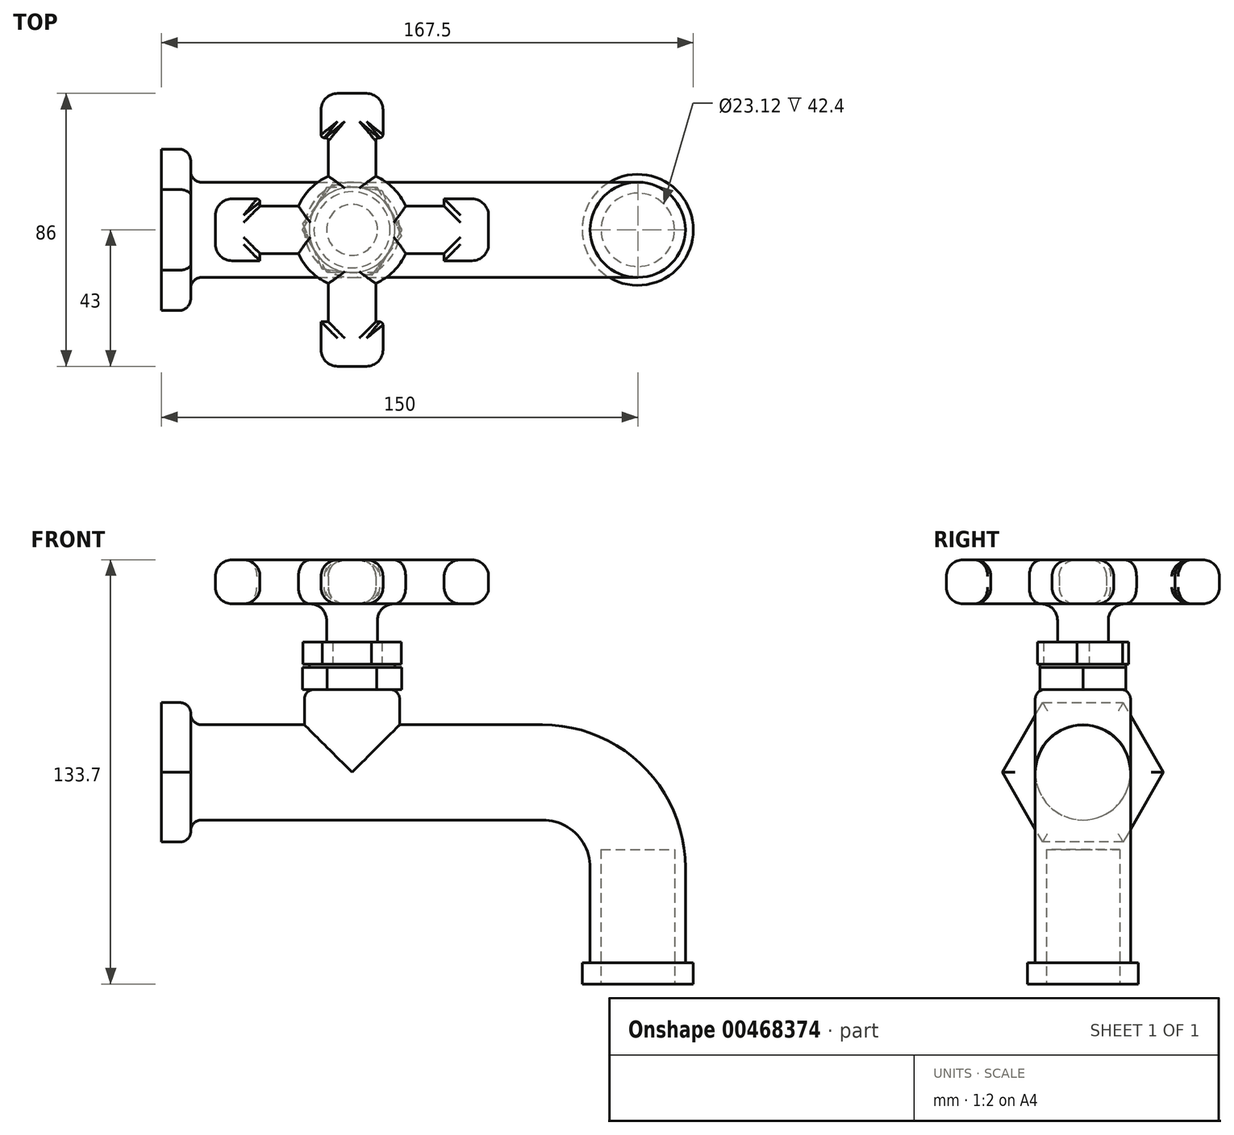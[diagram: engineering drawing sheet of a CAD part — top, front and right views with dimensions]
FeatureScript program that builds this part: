
annotation { "Feature Type Name" : "Feature", "Feature Type Description" : "" }
export const myFeature = defineFeature(function(context is Context, id is Id, definition is map)
    precondition{}
    {
        {
            var Q0;
            Q0=qCreatedBy(makeId("Front.planeOp"),FACE);
            var sketch = newSketch(context, id + "F0", { "sketchPlane" : qUnion([Q0])});
            skLineSegment(sketch, "E0", {"start": v(-60, 0) * mm, "end": v(60, 0) * mm});
            skLineSegment(sketch, "E1", {"start": v(90, -30) * mm, "end": v(90, -60) * mm});
            skPoint(sketch, "E2.visualSharp", {"position": v(90, 0) * mm});
            skArc(sketch, "E2.filletArc", {"start": v(90, -30) * mm, "mid": v(81.21, -8.79) * mm, "end": v(60, 0) * mm});
            skSolve(sketch);
        }
        {
            var Q0;
            Q0=sQuery(id+"F0.wireOp",VERTEX,"E0.start");
            var Q1;
            Q1=qCreatedBy(makeId("Right.planeOp"),FACE);
            cPlane(context, id + "F1", {"entities" : qUnion([Q0, Q1]), "cplaneType" : CPlaneType.PLANE_POINT, "offset" : 25 * mm, "width" : 150 * mm, "height" : 150 * mm});
        }
        {
            var Q0;
            Q0=qCreatedBy(id+"F1.planeOp",FACE);
            var sketch = newSketch(context, id + "F2", { "sketchPlane" : qUnion([Q0])});
            skCircle(sketch, "E3", {"center": v(0, 0) * mm, "radius": 15 * mm});
            skSolve(sketch);
        }
        {
            var Q0;
            Q0=makeQuery(id+"F2.imprint","IMPRINT",FACE,{"disambiguationData":[TD([[makeQuery(id+"F2.imprint","IMPRINT",EDGE,{"derivedFrom":sQuery(id+"F2.wireOp",EDGE,"E3")}),1.0]])]});
            var Q1;
            Q1=sQuery(id+"F0.wireOp",EDGE,"E0");
            var Q2;
            Q2=sQuery(id+"F0.wireOp",EDGE,"E2.filletArc");
            var Q3;
            Q3=sQuery(id+"F0.wireOp",EDGE,"E1");
            sweep(context, id + "F3", {"profiles" : qUnion([Q0]), "path" : qUnion([Q1, Q2, Q3])});
        }
        {
            var Q0;
            Q0=qCreatedBy(makeId("Top.planeOp"),FACE);
            var sketch = newSketch(context, id + "F4", { "sketchPlane" : qUnion([Q0])});
            skLineSegment(sketch, "E4.0", {"start": v(-60, 0) * mm, "end": v(60, 0) * mm, "construction": true});
            skCircle(sketch, "E5", {"center": v(0, 0) * mm, "radius": 15 * mm});
            skSolve(sketch);
        }
        {
            var Q0;
            Q0 = qSketchRegion(id + "F4", true);
            extrude(context, id + "F5", {"entities" : qUnion([Q0]), "operationType" : NewBodyOperationType.ADD, "depth" : 26.1 * mm});
        }
        {
            var Q0;
            Q0=makeQuery(id+"F5.opExtrude","CAP_FACE",FACE,{"disambiguationData":[OSD([sQuery(id+"F4.wireOp",EDGE,"E5")])],"isStart":false});
            fillet(context, id + "F6", {"entities" : qUnion([Q0]), "radius" : 3 * mm, "tangentPropagation" : true, "allowEdgeOverflow" : false});
        }
        {
            var Q0;
            Q0=makeQuery(id+"F5.opExtrude","CAP_FACE",FACE,{"disambiguationData":[OSD([sQuery(id+"F4.wireOp",EDGE,"E5")])],"isStart":false});
            var sketch = newSketch(context, id + "F7", { "sketchPlane" : qUnion([Q0])});
            skCircle(sketch, "E6.cCircle", {"center": v(0, 0) * mm, "radius": 13.5 * mm, "construction": true});
            skLineSegment(sketch, "E6.0", {"start": v(15.59, 0) * mm, "end": v(7.8, -13.5) * mm});
            skLineSegment(sketch, "E6.1", {"start": v(7.8, -13.5) * mm, "end": v(-7.8, -13.5) * mm});
            skLineSegment(sketch, "E6.2", {"start": v(-7.8, -13.5) * mm, "end": v(-15.59, 0) * mm});
            skLineSegment(sketch, "E6.3", {"start": v(-15.59, 0) * mm, "end": v(-7.8, 13.5) * mm});
            skLineSegment(sketch, "E6.4", {"start": v(-7.8, 13.5) * mm, "end": v(7.8, 13.5) * mm});
            skLineSegment(sketch, "E6.5", {"start": v(7.8, 13.5) * mm, "end": v(15.59, 0) * mm});
            skPoint(sketch, "E6.0.midPoint", {"position": v(11.7, -6.75) * mm});
            skSolve(sketch);
        }
        {
            var Q0;
            Q0 = qSketchRegion(id + "F7", true);
            extrude(context, id + "F8", {"entities" : qUnion([Q0]), "operationType" : NewBodyOperationType.ADD, "depth" : 7 * mm});
        }
        {
            var Q0;
            Q0=makeQuery(id+"F8.opExtrude","CAP_FACE",FACE,{"disambiguationData":[OSD([sQuery(id+"F7.wireOp",EDGE,"E6.0"),sQuery(id+"F7.wireOp",EDGE,"E6.1"),sQuery(id+"F7.wireOp",EDGE,"E6.2"),sQuery(id+"F7.wireOp",EDGE,"E6.3"),sQuery(id+"F7.wireOp",EDGE,"E6.4"),sQuery(id+"F7.wireOp",EDGE,"E6.5")])],"isStart":false});
            var sketch = newSketch(context, id + "F9", { "sketchPlane" : qUnion([Q0])});
            skCircle(sketch, "E7.0", {"center": v(0, 0) * mm, "radius": 13.5 * mm});
            skSolve(sketch);
        }
        {
            var Q0;
            Q0 = qSketchRegion(id + "F9", true);
            extrude(context, id + "F10", {"entities" : qUnion([Q0]), "operationType" : NewBodyOperationType.ADD, "depth" : 1 * mm});
        }
        {
            var Q0;
            Q0=makeQuery(id+"F10.opExtrude","CAP_FACE",FACE,{"disambiguationData":[OSD([sQuery(id+"F9.wireOp",EDGE,"E7.0")])],"isStart":false});
            var sketch = newSketch(context, id + "F11", { "sketchPlane" : qUnion([Q0])});
            skCircle(sketch, "E8.cCircle", {"center": v(0, 0) * mm, "radius": 13.5 * mm, "construction": true});
            skLineSegment(sketch, "E8.0", {"start": v(9.38, 12.45) * mm, "end": v(15.47, -1.9) * mm});
            skLineSegment(sketch, "E8.1", {"start": v(15.47, -1.9) * mm, "end": v(6.1, -14.35) * mm});
            skLineSegment(sketch, "E8.2", {"start": v(6.1, -14.35) * mm, "end": v(-9.38, -12.45) * mm});
            skLineSegment(sketch, "E8.3", {"start": v(-9.38, -12.45) * mm, "end": v(-15.47, 1.9) * mm});
            skLineSegment(sketch, "E8.4", {"start": v(-15.47, 1.9) * mm, "end": v(-6.1, 14.35) * mm});
            skLineSegment(sketch, "E8.5", {"start": v(-6.1, 14.35) * mm, "end": v(9.38, 12.45) * mm});
            skPoint(sketch, "E8.0.midPoint", {"position": v(12.42, 5.28) * mm});
            skSolve(sketch);
        }
        {
            var Q0;
            Q0 = qSketchRegion(id + "F11", true);
            extrude(context, id + "F12", {"entities" : qUnion([Q0]), "operationType" : NewBodyOperationType.ADD, "depth" : 7 * mm});
        }
        {
            var Q0;
            Q0=makeQuery(id+"F12.opExtrude","CAP_FACE",FACE,{"disambiguationData":[OSD([sQuery(id+"F11.wireOp",EDGE,"E8.0"),sQuery(id+"F11.wireOp",EDGE,"E8.1"),sQuery(id+"F11.wireOp",EDGE,"E8.2"),sQuery(id+"F11.wireOp",EDGE,"E8.3"),sQuery(id+"F11.wireOp",EDGE,"E8.4"),sQuery(id+"F11.wireOp",EDGE,"E8.5")])],"isStart":false});
            var sketch = newSketch(context, id + "F13", { "sketchPlane" : qUnion([Q0])});
            skCircle(sketch, "E9", {"center": v(0, 0) * mm, "radius": 8 * mm});
            skSolve(sketch);
        }
        {
            var Q0;
            Q0 = qSketchRegion(id + "F13", true);
            extrude(context, id + "F14", {"entities" : qUnion([Q0]), "operationType" : NewBodyOperationType.ADD, "depth" : 12 * mm});
        }
        {
            var Q0;
            Q0=makeQuery(id+"F14.opExtrude","CAP_FACE",FACE,{"disambiguationData":[OSD([sQuery(id+"F13.wireOp",EDGE,"E9")])],"isStart":false});
            var sketch = newSketch(context, id + "F15", { "sketchPlane" : qUnion([Q0])});
            skPoint(sketch, "E10.middle", {"position": v(0, 0) * mm});
            skLineSegment(sketch, "E11.bottom", {"start": v(-29, 7.47) * mm, "end": v(-16.88, 7.47) * mm});
            skLineSegment(sketch, "E11.top", {"start": v(-29, -7.47) * mm, "end": v(-16.88, -7.47) * mm});
            skLineSegment(sketch, "E12.left", {"start": v(-43, 9.74) * mm, "end": v(-43, -9.74) * mm});
            skLineSegment(sketch, "E12.right", {"start": v(-29, 9.74) * mm, "end": v(-29, 7.47) * mm});
            skLineSegment(sketch, "E13.left", {"start": v(43, 9.74) * mm, "end": v(43, -9.74) * mm});
            skLineSegment(sketch, "E13.right", {"start": v(29, 9.74) * mm, "end": v(29, 7.47) * mm});
            skArc(sketch, "E14", {"start": v(-16.88, -7.47) * mm, "mid": v(-13.05, -13.05) * mm, "end": v(-7.47, -16.88) * mm});
            skLineSegment(sketch, "E15.trimOffspring", {"start": v(16.88, 7.47) * mm, "end": v(29, 7.47) * mm});
            skLineSegment(sketch, "E16.trimOffspring", {"start": v(16.88, -7.47) * mm, "end": v(29, -7.47) * mm});
            skArc(sketch, "E17.trimOffspring", {"start": v(16.88, 7.47) * mm, "mid": v(13.05, 13.05) * mm, "end": v(7.47, 16.88) * mm});
            skLineSegment(sketch, "E18.trimOffspring", {"start": v(-29, -7.47) * mm, "end": v(-29, -9.74) * mm});
            skLineSegment(sketch, "E19.1.0", {"start": v(-7.47, -16.88) * mm, "end": v(-7.47, -29) * mm});
            skLineSegment(sketch, "E19.1.1", {"start": v(7.47, -16.88) * mm, "end": v(7.47, -29) * mm});
            skLineSegment(sketch, "E19.1.2", {"start": v(9.74, 43) * mm, "end": v(-9.74, 43) * mm});
            skLineSegment(sketch, "E19.1.4", {"start": v(9.74, -29) * mm, "end": v(7.47, -29) * mm});
            skArc(sketch, "E19.1.5", {"start": v(-7.47, 16.88) * mm, "mid": v(-13.05, 13.05) * mm, "end": v(-16.88, 7.47) * mm});
            skLineSegment(sketch, "E19.1.7", {"start": v(9.74, 29) * mm, "end": v(7.47, 29) * mm});
            skLineSegment(sketch, "E19.1.9", {"start": v(-7.47, 29) * mm, "end": v(-9.74, 29) * mm});
            skLineSegment(sketch, "E19.1.10", {"start": v(-7.47, 29) * mm, "end": v(-7.47, 16.88) * mm});
            skLineSegment(sketch, "E19.1.11", {"start": v(7.47, 29) * mm, "end": v(7.47, 16.88) * mm});
            skArc(sketch, "E19.1.18", {"start": v(7.47, -16.88) * mm, "mid": v(13.05, -13.05) * mm, "end": v(16.88, -7.47) * mm});
            skLineSegment(sketch, "E19.1.19", {"start": v(9.74, -43) * mm, "end": v(-9.74, -43) * mm});
            skLineSegment(sketch, "E19.1.20", {"start": v(-7.27, -29) * mm, "end": v(-9.74, -29) * mm});
            skLineSegment(sketch, "E19.1.23", {"start": v(-9.74, -29) * mm, "end": v(-7.27, -29) * mm});
            skLineSegment(sketch, "E19.anchor1", {"start": v(0, 0) * mm, "end": v(-43, -13) * mm, "construction": true});
            skLineSegment(sketch, "E19.anchor2", {"start": v(0, 0) * mm, "end": v(-13, 43) * mm, "construction": true});
            skLineSegment(sketch, "E20", {"start": v(29, -7.47) * mm, "end": v(29, -9.74) * mm});
            skLineSegment(sketch, "E21.bottom", {"start": v(43, 9.74) * mm, "end": v(29, 9.74) * mm});
            skLineSegment(sketch, "E21.top", {"start": v(43, -9.74) * mm, "end": v(29, -9.74) * mm});
            skLineSegment(sketch, "E22.trimOffspring", {"start": v(-29, 9.74) * mm, "end": v(-43, 9.74) * mm});
            skLineSegment(sketch, "E23.trimOffspring", {"start": v(-29, -9.74) * mm, "end": v(-43, -9.74) * mm});
            skLineSegment(sketch, "E24.left", {"start": v(9.74, 43) * mm, "end": v(9.74, 29) * mm});
            skLineSegment(sketch, "E24.right", {"start": v(-9.74, 43) * mm, "end": v(-9.74, 29) * mm});
            skLineSegment(sketch, "E25.trimOffspring", {"start": v(-9.74, -29) * mm, "end": v(-9.74, -43) * mm});
            skLineSegment(sketch, "E26.trimOffspring", {"start": v(9.74, -29) * mm, "end": v(9.74, -43) * mm});
            skSolve(sketch);
        }
        {
            var Q0;
            Q0 = qSketchRegion(id + "F15", true);
            extrude(context, id + "F16", {"entities" : qUnion([Q0]), "operationType" : NewBodyOperationType.ADD, "depth" : 13.9 * mm});
        }
        {
            var Q0;
            Q0=makeQuery(id+"F16.opExtrude","CAP_FACE",FACE,{"disambiguationData":[OSD([sQuery(id+"F15.wireOp",EDGE,"E11.bottom"),sQuery(id+"F15.wireOp",EDGE,"E11.top"),sQuery(id+"F15.wireOp",EDGE,"E12.right"),sQuery(id+"F15.wireOp",EDGE,"E13.right"),sQuery(id+"F15.wireOp",EDGE,"E15.trimOffspring"),sQuery(id+"F15.wireOp",EDGE,"E16.trimOffspring"),sQuery(id+"F15.wireOp",EDGE,"E18.trimOffspring"),sQuery(id+"F15.wireOp",EDGE,"E19.1.0"),sQuery(id+"F15.wireOp",EDGE,"E19.1.1"),sQuery(id+"F15.wireOp",EDGE,"E19.1.2"),sQuery(id+"F15.wireOp",EDGE,"E19.1.4"),sQuery(id+"F15.wireOp",EDGE,"E19.1.7"),sQuery(id+"F15.wireOp",EDGE,"E19.1.9"),sQuery(id+"F15.wireOp",EDGE,"E19.1.10"),sQuery(id+"F15.wireOp",EDGE,"E19.1.11"),sQuery(id+"F15.wireOp",EDGE,"E19.1.19"),sQuery(id+"F15.wireOp",EDGE,"E19.1.23"),sQuery(id+"F15.wireOp",EDGE,"E19.1.5"),sQuery(id+"F15.wireOp",EDGE,"E17.trimOffspring"),sQuery(id+"F15.wireOp",EDGE,"E19.1.18"),sQuery(id+"F15.wireOp",EDGE,"E14"),sQuery(id+"F15.wireOp",EDGE,"E20"),sQuery(id+"F15.wireOp",EDGE,"E21.bottom"),sQuery(id+"F15.wireOp",EDGE,"E21.top"),sQuery(id+"F15.wireOp",EDGE,"E13.left"),sQuery(id+"F15.wireOp",EDGE,"E12.left"),sQuery(id+"F15.wireOp",EDGE,"E22.trimOffspring"),sQuery(id+"F15.wireOp",EDGE,"E23.trimOffspring"),sQuery(id+"F15.wireOp",EDGE,"E24.left"),sQuery(id+"F15.wireOp",EDGE,"E24.right"),sQuery(id+"F15.wireOp",EDGE,"E25.trimOffspring"),sQuery(id+"F15.wireOp",EDGE,"E26.trimOffspring")])],"isStart":true});
            var Q1;
            Q1=makeQuery(id+"F16.opExtrude","CAP_FACE",FACE,{"disambiguationData":[OSD([sQuery(id+"F15.wireOp",EDGE,"E11.bottom"),sQuery(id+"F15.wireOp",EDGE,"E11.top"),sQuery(id+"F15.wireOp",EDGE,"E12.right"),sQuery(id+"F15.wireOp",EDGE,"E13.right"),sQuery(id+"F15.wireOp",EDGE,"E15.trimOffspring"),sQuery(id+"F15.wireOp",EDGE,"E16.trimOffspring"),sQuery(id+"F15.wireOp",EDGE,"E18.trimOffspring"),sQuery(id+"F15.wireOp",EDGE,"E19.1.0"),sQuery(id+"F15.wireOp",EDGE,"E19.1.1"),sQuery(id+"F15.wireOp",EDGE,"E19.1.2"),sQuery(id+"F15.wireOp",EDGE,"E19.1.4"),sQuery(id+"F15.wireOp",EDGE,"E19.1.7"),sQuery(id+"F15.wireOp",EDGE,"E19.1.9"),sQuery(id+"F15.wireOp",EDGE,"E19.1.10"),sQuery(id+"F15.wireOp",EDGE,"E19.1.11"),sQuery(id+"F15.wireOp",EDGE,"E19.1.19"),sQuery(id+"F15.wireOp",EDGE,"E19.1.23"),sQuery(id+"F15.wireOp",EDGE,"E19.1.5"),sQuery(id+"F15.wireOp",EDGE,"E17.trimOffspring"),sQuery(id+"F15.wireOp",EDGE,"E19.1.18"),sQuery(id+"F15.wireOp",EDGE,"E14"),sQuery(id+"F15.wireOp",EDGE,"E20"),sQuery(id+"F15.wireOp",EDGE,"E21.bottom"),sQuery(id+"F15.wireOp",EDGE,"E21.top"),sQuery(id+"F15.wireOp",EDGE,"E13.left"),sQuery(id+"F15.wireOp",EDGE,"E12.left"),sQuery(id+"F15.wireOp",EDGE,"E22.trimOffspring"),sQuery(id+"F15.wireOp",EDGE,"E23.trimOffspring"),sQuery(id+"F15.wireOp",EDGE,"E24.left"),sQuery(id+"F15.wireOp",EDGE,"E24.right"),sQuery(id+"F15.wireOp",EDGE,"E25.trimOffspring"),sQuery(id+"F15.wireOp",EDGE,"E26.trimOffspring")])],"isStart":false});
            var Q2;
            Q2=makeQuery(id+"F16.opExtrude","SWEPT_FACE",FACE,{"disambiguationData":[OSD([sQuery(id+"F15.wireOp",EDGE,"E19.1.19")])]});
            var Q3;
            Q3=makeQuery(id+"F16.opExtrude","SWEPT_FACE",FACE,{"disambiguationData":[OSD([sQuery(id+"F15.wireOp",EDGE,"E12.left")])]});
            var Q4;
            Q4=makeQuery(id+"F16.opExtrude","SWEPT_FACE",FACE,{"disambiguationData":[OSD([sQuery(id+"F15.wireOp",EDGE,"E19.1.2")])]});
            var Q5;
            Q5=makeQuery(id+"F16.opExtrude","SWEPT_FACE",FACE,{"disambiguationData":[OSD([sQuery(id+"F15.wireOp",EDGE,"E13.left")])]});
            fillet(context, id + "F17", {"entities" : qUnion([Q0, Q1, Q2, Q3, Q4, Q5]), "radius" : 5.2 * mm, "tangentPropagation" : true, "allowEdgeOverflow" : false});
        }
        {
            var Q0;
            {var subQ0=sQuery(id+"F15.wireOp",EDGE,"E22.trimOffspring");Q0=makeQuery(id+"F17.opFillet","BLEND_FACE",FACE,{"disambiguationData":[OSD([subQ0]),TDD([makeQuery(id+"F16.opExtrude","CAP_EDGE",EDGE,{"disambiguationData":[OSD([subQ0])],"isStart":false})])]});}
            var Q1;
            {var subQ0=sQuery(id+"F15.wireOp",EDGE,"E26.trimOffspring");Q1=makeQuery(id+"F17.opFillet","BLEND_FACE",FACE,{"disambiguationData":[OSD([subQ0]),TDD([makeQuery(id+"F16.opExtrude","CAP_EDGE",EDGE,{"disambiguationData":[OSD([subQ0])],"isStart":false})])]});}
            var Q2;
            Q2=makeQuery(id+"F16.opExtrude","SWEPT_FACE",FACE,{"disambiguationData":[OSD([sQuery(id+"F15.wireOp",EDGE,"E19.1.7")])]});
            var Q3;
            {var subQ0=sQuery(id+"F15.wireOp",EDGE,"E19.1.9");Q3=makeQuery(id+"F17.opFillet","BLEND_FACE",FACE,{"disambiguationData":[OSD([subQ0]),TDD([makeQuery(id+"F16.opExtrude","CAP_EDGE",EDGE,{"disambiguationData":[OSD([subQ0])],"isStart":true})])]});}
            var Q4;
            {var subQ0=sQuery(id+"F15.wireOp",EDGE,"E19.1.9");Q4=makeQuery(id+"F17.opFillet","BLEND_FACE",FACE,{"disambiguationData":[OSD([subQ0]),TDD([makeQuery(id+"F16.opExtrude","CAP_EDGE",EDGE,{"disambiguationData":[OSD([subQ0])],"isStart":false})])]});}
            fillet(context, id + "F18", {"entities" : qUnion([Q0, Q1, Q2, Q3, Q4]), "radius" : 1 * mm, "tangentPropagation" : true, "allowEdgeOverflow" : false});
        }
        {
            var Q0;
            Q0=makeQuery(id+"F2.imprint","IMPRINT",FACE,{"disambiguationData":[TD([[makeQuery(id+"F2.imprint","IMPRINT",EDGE,{"derivedFrom":sQuery(id+"F2.wireOp",EDGE,"E3")}),1.0]])]});
            var sketch = newSketch(context, id + "F19", { "sketchPlane" : qUnion([Q0])});
            skCircle(sketch, "E27.cCircle", {"center": v(0, 0) * mm, "radius": 21.98 * mm, "construction": true});
            skLineSegment(sketch, "E27.0", {"start": v(-12.69, -21.98) * mm, "end": v(-25.38, 0) * mm});
            skLineSegment(sketch, "E27.1", {"start": v(-25.38, 0) * mm, "end": v(-12.69, 21.98) * mm});
            skLineSegment(sketch, "E27.2", {"start": v(-12.69, 21.98) * mm, "end": v(12.69, 21.98) * mm});
            skLineSegment(sketch, "E27.3", {"start": v(12.69, 21.98) * mm, "end": v(25.38, 0) * mm});
            skLineSegment(sketch, "E27.4", {"start": v(25.38, 0) * mm, "end": v(12.69, -21.98) * mm});
            skLineSegment(sketch, "E27.5", {"start": v(12.69, -21.98) * mm, "end": v(-12.69, -21.98) * mm});
            skPoint(sketch, "E27.0.midPoint", {"position": v(-19.03, -10.99) * mm});
            skSolve(sketch);
        }
        {
            var Q0;
            Q0 = qSketchRegion(id + "F19", true);
            extrude(context, id + "F20", {"entities" : qUnion([Q0]), "operationType" : NewBodyOperationType.ADD, "depth" : 9.2 * mm});
        }
        {
            var Q0;
            Q0=makeQuery(id+"F20.opExtrude","CAP_FACE",FACE,{"disambiguationData":[OSD([sQuery(id+"F19.wireOp",EDGE,"E27.0"),sQuery(id+"F19.wireOp",EDGE,"E27.1"),sQuery(id+"F19.wireOp",EDGE,"E27.2"),sQuery(id+"F19.wireOp",EDGE,"E27.3"),sQuery(id+"F19.wireOp",EDGE,"E27.4"),sQuery(id+"F19.wireOp",EDGE,"E27.5")])],"isStart":false});
            fillet(context, id + "F21", {"entities" : qUnion([Q0]), "radius" : 3.4 * mm, "tangentPropagation" : true, "allowEdgeOverflow" : false});
        }
        {
            var Q0;
            Q0=makeQuery(id+"F3.opSweep","CAP_FACE",FACE,{"disambiguationData":[OSD([sQuery(id+"F0.wireOp",VERTEX,"E1.end"),sQuery(id+"F2.wireOp",EDGE,"E3")])],"isStart":false});
            var sketch = newSketch(context, id + "F22", { "sketchPlane" : qUnion([Q0])});
            skCircle(sketch, "E28", {"center": v(90, 0) * mm, "radius": 17.5 * mm});
            skSolve(sketch);
        }
        {
            var Q0;
            Q0 = qSketchRegion(id + "F22", true);
            extrude(context, id + "F23", {"entities" : qUnion([Q0]), "operationType" : NewBodyOperationType.ADD, "depth" : 6.7 * mm});
        }
        {
            var Q0;
            Q0=makeQuery(id+"F23.opExtrude","CAP_FACE",FACE,{"disambiguationData":[OSD([sQuery(id+"F22.wireOp",EDGE,"E28")])],"isStart":false});
            var sketch = newSketch(context, id + "F24", { "sketchPlane" : qUnion([Q0])});
            skCircle(sketch, "E29", {"center": v(90, 0) * mm, "radius": 11.56 * mm});
            skSolve(sketch);
        }
        {
            var Q0;
            Q0 = qSketchRegion(id + "F24", true);
            extrude(context, id + "F25", {"entities" : qUnion([Q0]), "operationType" : NewBodyOperationType.REMOVE, "oppositeDirection" : true, "depth" : 42.4 * mm});
        }
    });
